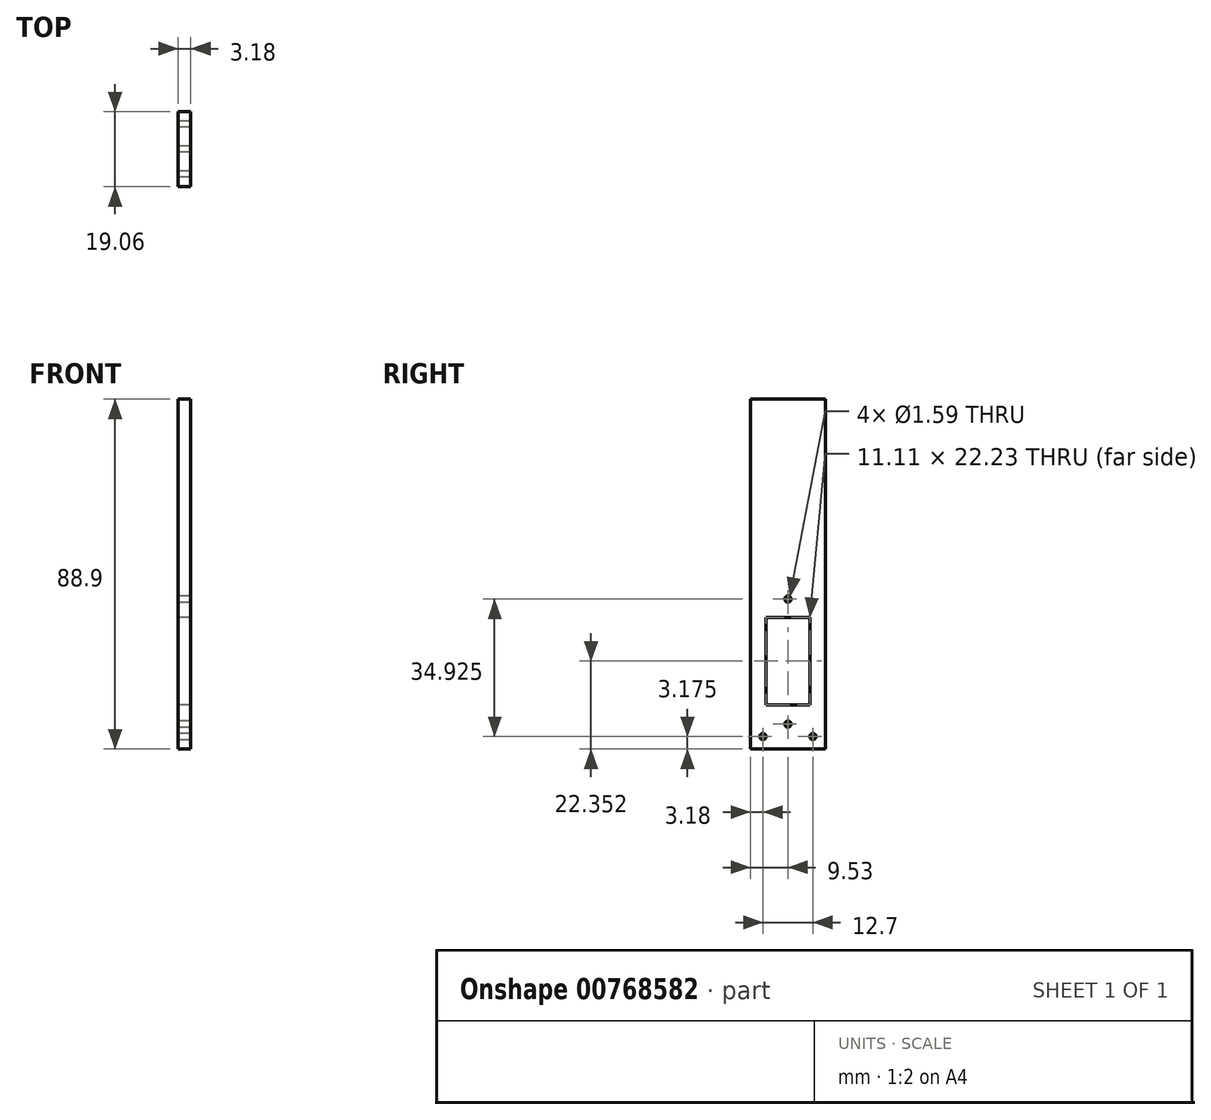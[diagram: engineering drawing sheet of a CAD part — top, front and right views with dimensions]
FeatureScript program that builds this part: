
annotation { "Feature Type Name" : "Feature", "Feature Type Description" : "" }
export const myFeature = defineFeature(function(context is Context, id is Id, definition is map)
    precondition{}
    {
        {
            var Q0;
            Q0=qCreatedBy(makeId("Right.planeOp"),FACE);
            var sketch = newSketch(context, id + "F0", { "sketchPlane" : qUnion([Q0])});
            skLineSegment(sketch, "E0.bottom", {"start": v(9.52, -44.45) * mm, "end": v(-9.53, -44.45) * mm});
            skLineSegment(sketch, "E0.top", {"start": v(9.53, 44.45) * mm, "end": v(-9.52, 44.45) * mm});
            skLineSegment(sketch, "E0.left", {"start": v(9.52, -44.45) * mm, "end": v(9.53, 44.45) * mm});
            skLineSegment(sketch, "E0.right", {"start": v(-9.53, -44.45) * mm, "end": v(-9.52, 44.45) * mm});
            skPoint(sketch, "E0.middle", {"position": v(0, 0) * mm});
            skPoint(sketch, "E1", {"position": v(0, 44.45) * mm});
            skPoint(sketch, "E2", {"position": v(-6.35, -44.45) * mm});
            skPoint(sketch, "E3", {"position": v(-9.53, -41.28) * mm});
            skCircle(sketch, "E4", {"center": v(-6.35, -41.28) * mm, "radius": 0.8 * mm});
            skCircle(sketch, "E5.MirrorC", {"center": v(6.35, -41.28) * mm, "radius": 0.8 * mm});
            skCircle(sketch, "E6", {"center": v(0, -38.1) * mm, "radius": 0.8 * mm});
            skCircle(sketch, "E7", {"center": v(0, -6.35) * mm, "radius": 0.8 * mm});
            skLineSegment(sketch, "E8.bottom", {"start": v(-5.56, -10.99) * mm, "end": v(5.56, -10.99) * mm});
            skLineSegment(sketch, "E8.top", {"start": v(-5.56, -33.21) * mm, "end": v(5.56, -33.21) * mm});
            skLineSegment(sketch, "E8.left", {"start": v(-5.56, -10.99) * mm, "end": v(-5.56, -33.21) * mm});
            skLineSegment(sketch, "E8.right", {"start": v(5.56, -10.99) * mm, "end": v(5.56, -33.21) * mm});
            skPoint(sketch, "E9.center.orphan", {"position": v(0, -12.7) * mm});
            skPoint(sketch, "E10", {"position": v(0, -10.99) * mm});
            skSolve(sketch);
        }
        {
            var Q0;
            Q0=makeQuery(id+"F0.imprint","IMPRINT",FACE,{"disambiguationData":[TD([[makeQuery(id+"F0.imprint","IMPRINT",EDGE,{"derivedFrom":sQuery(id+"F0.wireOp",EDGE,"E0.bottom")}),-1.0]])]});
            extrude(context, id + "F1", {"entities" : qUnion([Q0]), "depth" : 3.17 * mm, "offsetDistance" : 25.4 * mm});
        }
    });
